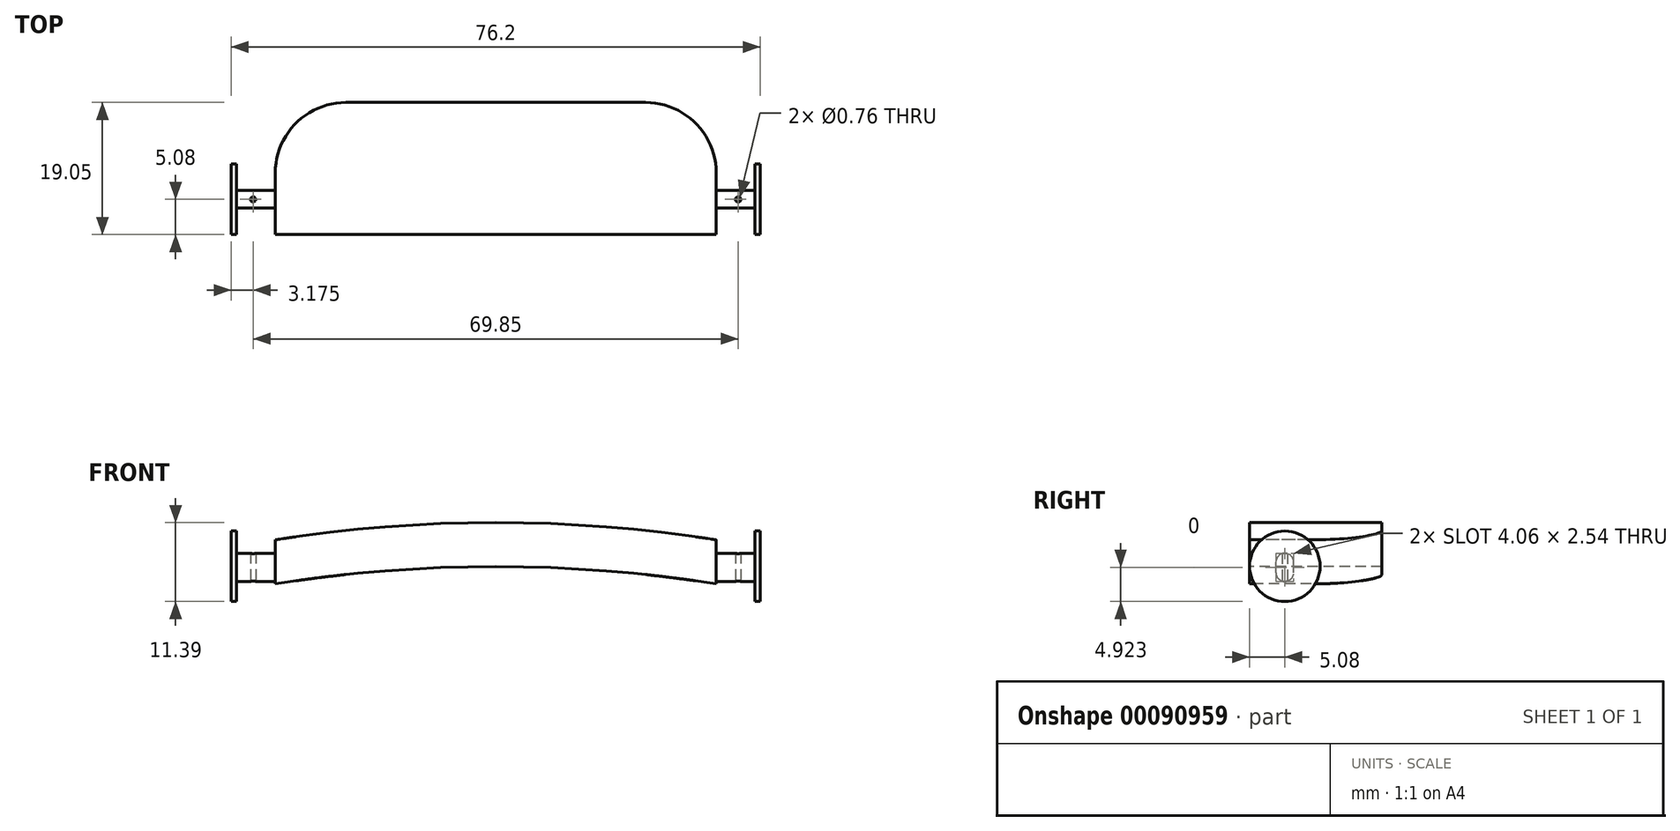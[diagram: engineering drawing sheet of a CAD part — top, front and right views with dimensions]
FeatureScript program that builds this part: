
annotation { "Feature Type Name" : "Feature", "Feature Type Description" : "" }
export const myFeature = defineFeature(function(context is Context, id is Id, definition is map)
    precondition{}
    {
        {
            var Q0;
            Q0=qCreatedBy(makeId("Front.planeOp"),FACE);
            var sketch = newSketch(context, id + "F0", { "sketchPlane" : qUnion([Q0])});
            skArc(sketch, "E0", {"start": v(31.75, 6.35) * mm, "mid": v(0, 8.85) * mm, "end": v(-31.75, 6.35) * mm});
            skLineSegment(sketch, "E1", {"start": v(-31.75, 6.35) * mm, "end": v(-31.75, 0) * mm});
            skLineSegment(sketch, "E2", {"start": v(31.75, 6.35) * mm, "end": v(31.75, 0) * mm});
            skArc(sketch, "E3", {"start": v(31.75, 0) * mm, "mid": v(0, 2.5) * mm, "end": v(-31.75, 0) * mm});
            skSolve(sketch);
        }
        {
            var Q0;
            Q0 = qSketchRegion(id + "F0", true);
            extrude(context, id + "F1", {"entities" : qUnion([Q0]), "oppositeDirection" : true, "depth" : 19.05 * mm});
        }
        {
            var Q0;
            Q0=makeQuery(id+"F1.opExtrude","CAP_EDGE",EDGE,{"disambiguationData":[OSD([sQuery(id+"F0.wireOp",EDGE,"E1")])],"isStart":false});
            var Q1;
            Q1=makeQuery(id+"F1.opExtrude","CAP_EDGE",EDGE,{"disambiguationData":[OSD([sQuery(id+"F0.wireOp",EDGE,"E2")])],"isStart":false});
            fillet(context, id + "F2", {"entities" : qUnion([Q0, Q1]), "radius" : 10.16 * mm, "tangentPropagation" : true, "allowEdgeOverflow" : false});
        }
        {
            var Q0;
            Q0=qCreatedBy(makeId("Right.planeOp"),FACE);
            cPlane(context, id + "F3", {"entities" : qUnion([Q0]), "cplaneType" : CPlaneType.OFFSET, "offset" : 31.75 * mm, "width" : 152.4 * mm, "height" : 152.4 * mm});
        }
        {
            var Q0;
            Q0=qCreatedBy(id+"F3.planeOp",FACE);
            var sketch = newSketch(context, id + "F4", { "sketchPlane" : qUnion([Q0])});
            skLineSegment(sketch, "E4", {"start": v(0, 0) * mm, "end": v(5.08, 0) * mm});
            skLineSegment(sketch, "E5", {"start": v(5.08, 0) * mm, "end": v(5.08, 2.54) * mm});
            skArc(sketch, "E6", {"start": v(6.35, 3.15) * mm, "mid": v(5.08, 4.42) * mm, "end": v(3.81, 3.15) * mm});
            skArc(sketch, "E7", {"start": v(3.81, 1.62) * mm, "mid": v(5.08, 0.35) * mm, "end": v(6.35, 1.62) * mm});
            skLineSegment(sketch, "E8", {"start": v(3.81, 1.62) * mm, "end": v(3.81, 3.15) * mm});
            skLineSegment(sketch, "E9", {"start": v(6.35, 1.62) * mm, "end": v(6.35, 3.15) * mm});
            skSolve(sketch);
        }
        {
            var Q0;
            Q0 = qSketchRegion(id + "F4", true);
            extrude(context, id + "F5", {"entities" : qUnion([Q0]), "operationType" : NewBodyOperationType.ADD, "depth" : 6.35 * mm});
        }
        {
            var Q0;
            Q0 = qSketchRegion(id + "F4", true);
            extrude(context, id + "F6", {"entities" : qUnion([Q0]), "operationType" : NewBodyOperationType.ADD, "oppositeDirection" : true, "depth" : 69.85 * mm});
        }
        {
            var Q0;
            Q0=qCreatedBy(makeId("Front.planeOp"),FACE);
            var sketch = newSketch(context, id + "F7", { "sketchPlane" : qUnion([Q0])});
            skArc(sketch, "E10", {"start": v(31.75, 0) * mm, "mid": v(0, 2.5) * mm, "end": v(-31.75, 0) * mm});
            skLineSegment(sketch, "E11", {"start": v(-31.75, 0) * mm, "end": v(31.75, 0) * mm});
            skPoint(sketch, "E12", {"position": v(0, 0) * mm});
            skSolve(sketch);
        }
        {
            var Q0;
            Q0 = qSketchRegion(id + "F7", true);
            extrude(context, id + "F8", {"entities" : qUnion([Q0]), "operationType" : NewBodyOperationType.REMOVE, "oppositeDirection" : true, "depth" : 25.4 * mm});
        }
        {
            var Q0;
            Q0=qCreatedBy(id+"F3.planeOp",FACE);
            cPlane(context, id + "F9", {"entities" : qUnion([Q0]), "cplaneType" : CPlaneType.OFFSET, "offset" : 69.85 * mm, "oppositeDirection" : true, "width" : 152.4 * mm, "height" : 152.4 * mm});
        }
        {
            var Q0;
            Q0=qCreatedBy(id+"F9.planeOp",FACE);
            var sketch = newSketch(context, id + "F10", { "sketchPlane" : qUnion([Q0])});
            skCircle(sketch, "E13", {"center": v(5.08, 2.54) * mm, "radius": 5.08 * mm});
            skSolve(sketch);
        }
        {
            var Q0;
            Q0 = qSketchRegion(id + "F10", true);
            extrude(context, id + "F11", {"entities" : qUnion([Q0]), "operationType" : NewBodyOperationType.ADD, "depth" : 0.76 * mm});
        }
        {
            var Q0;
            Q0=qCreatedBy(id+"F3.planeOp",FACE);
            cPlane(context, id + "F12", {"entities" : qUnion([Q0]), "cplaneType" : CPlaneType.OFFSET, "offset" : 6.35 * mm, "width" : 152.4 * mm, "height" : 152.4 * mm});
        }
        {
            var Q0;
            Q0=qCreatedBy(id+"F12.planeOp",FACE);
            var sketch = newSketch(context, id + "F13", { "sketchPlane" : qUnion([Q0])});
            skCircle(sketch, "E14", {"center": v(5.08, 2.54) * mm, "radius": 5.08 * mm});
            skSolve(sketch);
        }
        {
            var Q0;
            Q0 = qSketchRegion(id + "F13", true);
            extrude(context, id + "F14", {"entities" : qUnion([Q0]), "operationType" : NewBodyOperationType.ADD, "oppositeDirection" : true, "depth" : 0.76 * mm});
        }
        {
            var Q0;
            Q0=qCreatedBy(makeId("Top.planeOp"),FACE);
            var sketch = newSketch(context, id + "F15", { "sketchPlane" : qUnion([Q0])});
            skCircle(sketch, "E15", {"center": v(34.93, 5.08) * mm, "radius": 0.38 * mm});
            skCircle(sketch, "E16", {"center": v(-34.93, 5.08) * mm, "radius": 0.38 * mm});
            skSolve(sketch);
        }
        {
            var Q0;
            Q0 = qSketchRegion(id + "F15", true);
            extrude(context, id + "F16", {"entities" : qUnion([Q0]), "operationType" : NewBodyOperationType.REMOVE, "depth" : 25.4 * mm});
        }
    });
